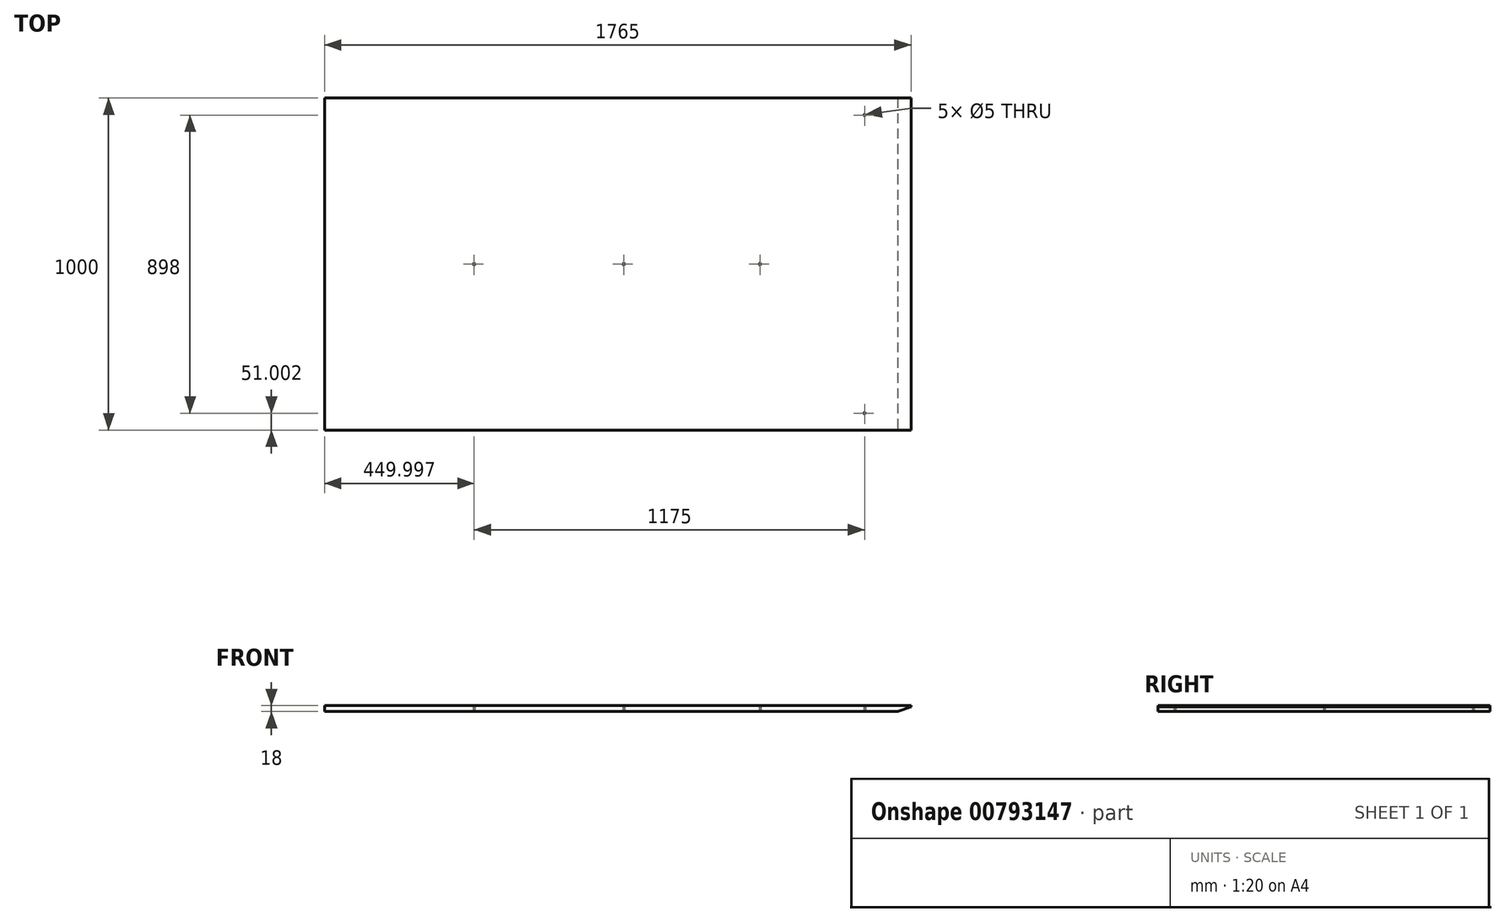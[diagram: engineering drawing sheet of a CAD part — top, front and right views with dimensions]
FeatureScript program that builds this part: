
annotation { "Feature Type Name" : "Feature", "Feature Type Description" : "" }
export const myFeature = defineFeature(function(context is Context, id is Id, definition is map)
    precondition{}
    {
        {
            var Q0;
            Q0=qCreatedBy(makeId("Top.planeOp"),FACE);
            var sketch = newSketch(context, id + "F0", { "sketchPlane" : qUnion([Q0])});
            skLineSegment(sketch, "E0.bottom", {"start": v(-1575.03, 957.65) * mm, "end": v(189.97, 957.65) * mm});
            skLineSegment(sketch, "E0.top", {"start": v(-1575.03, -42.35) * mm, "end": v(189.97, -42.35) * mm});
            skLineSegment(sketch, "E0.left", {"start": v(-1575.03, 957.65) * mm, "end": v(-1575.03, -42.35) * mm});
            skLineSegment(sketch, "E0.right", {"start": v(189.97, 957.65) * mm, "end": v(189.97, -42.35) * mm});
            skSolve(sketch);
        }
        {
            var Q0;
            Q0=makeQuery(id+"F0.imprint","IMPRINT",FACE,{"disambiguationData":[TD([[makeQuery(id+"F0.imprint","IMPRINT",EDGE,{"derivedFrom":sQuery(id+"F0.wireOp",EDGE,"E0.bottom")}),-1.0]])]});
            extrude(context, id + "F1", {"entities" : qUnion([Q0]), "depth" : 18 * mm, "offsetDistance" : 25 * mm});
        }
        {
            var Q0;
            Q0=makeQuery(id+"F1.opExtrude","SWEPT_FACE",FACE,{"disambiguationData":[OSD([sQuery(id+"F0.wireOp",EDGE,"E0.top")])]});
            var sketch = newSketch(context, id + "F2", { "sketchPlane" : qUnion([Q0])});
            skLineSegment(sketch, "E1", {"start": v(189.97, 14) * mm, "end": v(149.97, 0) * mm});
            skLineSegment(sketch, "E2", {"start": v(149.97, 0) * mm, "end": v(189.97, 0) * mm});
            skLineSegment(sketch, "E3", {"start": v(189.97, 0) * mm, "end": v(189.97, 14) * mm});
            skSolve(sketch);
        }
        {
            var Q0;
            Q0 = qSketchRegion(id + "F2", true);
            extrude(context, id + "F3", {"entities" : qUnion([Q0]), "operationType" : NewBodyOperationType.REMOVE, "endBound" : BoundingType.THROUGH_ALL, "oppositeDirection" : true, "depth" : 25 * mm, "offsetDistance" : 25 * mm});
        }
        {
            var Q0;
            Q0=makeQuery(id+"F1.opExtrude","CAP_FACE",FACE,{"disambiguationData":[OSD([sQuery(id+"F0.wireOp",EDGE,"E0.bottom"),sQuery(id+"F0.wireOp",EDGE,"E0.top"),sQuery(id+"F0.wireOp",EDGE,"E0.left"),sQuery(id+"F0.wireOp",EDGE,"E0.right")])],"isStart":true});
            var sketch = newSketch(context, id + "F4", { "sketchPlane" : qUnion([Q0])});
            skCircle(sketch, "E4", {"center": v(49.97, -8.65) * mm, "radius": 2.5 * mm});
            skCircle(sketch, "E5", {"center": v(49.97, -906.65) * mm, "radius": 2.5 * mm});
            skCircle(sketch, "E6", {"center": v(-675.03, -457.65) * mm, "radius": 2.5 * mm});
            skPoint(sketch, "E6.centerSnap0", {"position": v(-1575.03, -457.65) * mm});
            skCircle(sketch, "E7", {"center": v(-265.03, -457.65) * mm, "radius": 2.5 * mm});
            skPoint(sketch, "E7.centerSnap0", {"position": v(149.97, -457.65) * mm});
            skCircle(sketch, "E8", {"center": v(-1125.03, -457.65) * mm, "radius": 2.5 * mm});
            skSolve(sketch);
        }
        {
            var Q0;
            Q0 = qSketchRegion(id + "F4", true);
            extrude(context, id + "F5", {"entities" : qUnion([Q0]), "operationType" : NewBodyOperationType.REMOVE, "oppositeDirection" : true, "depth" : 25 * mm, "offsetDistance" : 25 * mm});
        }
    });
